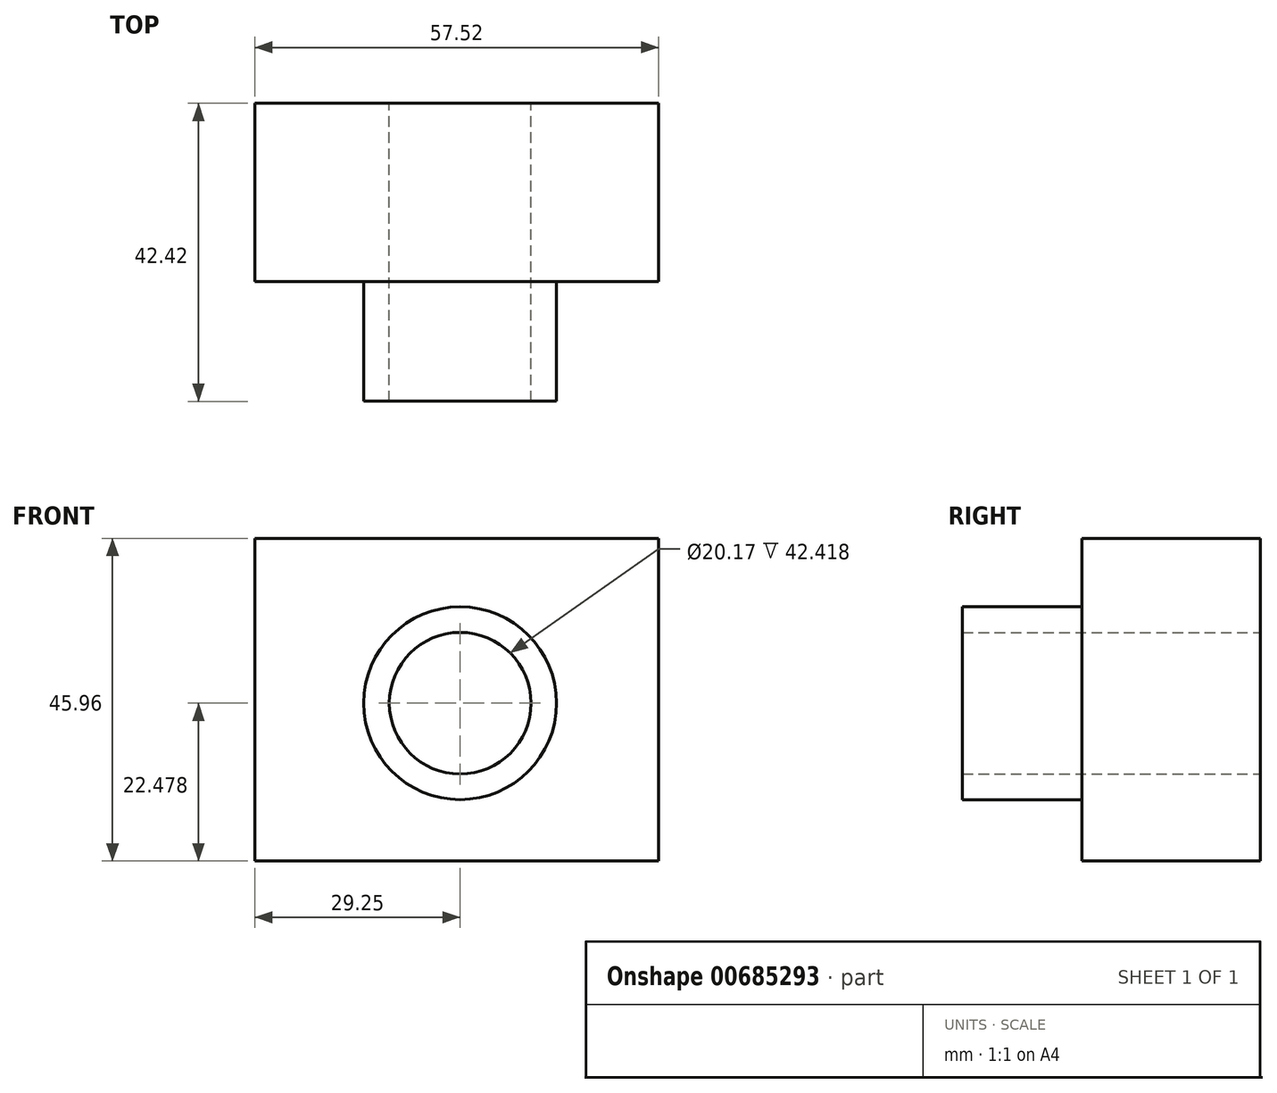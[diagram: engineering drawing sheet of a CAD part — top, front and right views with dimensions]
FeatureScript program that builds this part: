
annotation { "Feature Type Name" : "Feature", "Feature Type Description" : "" }
export const myFeature = defineFeature(function(context is Context, id is Id, definition is map)
    precondition{}
    {
        {
            var Q0;
            Q0=qCreatedBy(makeId("Front.planeOp"),FACE);
            var sketch = newSketch(context, id + "F0", { "sketchPlane" : qUnion([Q0])});
            skLineSegment(sketch, "E0.bottom", {"start": v(0, 0) * mm, "end": v(57.52, 0) * mm});
            skLineSegment(sketch, "E0.top", {"start": v(0, 45.96) * mm, "end": v(57.52, 45.96) * mm});
            skLineSegment(sketch, "E0.left", {"start": v(0, 0) * mm, "end": v(0, 45.96) * mm});
            skLineSegment(sketch, "E0.right", {"start": v(57.52, 0) * mm, "end": v(57.52, 45.96) * mm});
            skCircle(sketch, "E1", {"center": v(29.25, 22.48) * mm, "radius": 13.73 * mm});
            skCircle(sketch, "E2", {"center": v(29.25, 22.48) * mm, "radius": 10.08 * mm});
            skSolve(sketch);
        }
        {
            var Q0;
            Q0=makeQuery(id+"F0.imprint","IMPRINT",FACE,{"disambiguationData":[TD([[makeQuery(id+"F0.imprint","IMPRINT",EDGE,{"derivedFrom":sQuery(id+"F0.wireOp",EDGE,"E0.bottom")}),1.0]])]});
            extrude(context, id + "F1", {"entities" : qUnion([Q0]), "depth" : 25.4 * mm, "offsetDistance" : 25.4 * mm});
        }
        {
            var Q0;
            Q0 = qSketchRegion(id + "F0", true);
            extrude(context, id + "F2", {"entities" : qUnion([Q0]), "operationType" : NewBodyOperationType.ADD, "depth" : 25.4 * mm, "offsetDistance" : 25.4 * mm});
        }
        {
            var Q0;
            Q0=makeQuery(id+"F0.imprint","IMPRINT",FACE,{"disambiguationData":[TD([[makeQuery(id+"F0.imprint","IMPRINT",EDGE,{"derivedFrom":sQuery(id+"F0.wireOp",EDGE,"E1")}),1.0]])]});
            extrude(context, id + "F3", {"entities" : qUnion([Q0]), "operationType" : NewBodyOperationType.ADD, "depth" : 42.42 * mm, "offsetDistance" : 25.4 * mm});
        }
    });
